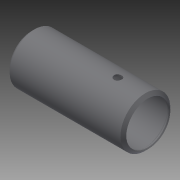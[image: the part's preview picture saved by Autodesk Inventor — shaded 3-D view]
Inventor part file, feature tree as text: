
AUTODESK INVENTOR PART (.ipt)
format: ipt  version: 2014 (Build 180170000, 170)  size: 142,336 bytes
history: native  units: in
note: dims shown in document units (in); Inventor stores cm internally (conversion verified against a paired STEP export)
features: other x56, revolve x2, sketch x2
ambient origin geometry x8: Origin, YZ Plane, XZ Plane, XY Plane, X Axis, Y Axis, Z Axis, Center Point
bodies: Solid1 (feature_tree)
feature tree (60):
  revolve  "Revolution1"  Angle=360.0deg
  revolve  "Revolution2"  [1 undecoded]
  other  "o1_XY"
  other  "o1_YZ"
  other  "o1_ZX"
  other  "o1_X"
  other  "o1_Y"
  other  "o1_Z"
  other  "o1_Center"
  other  "o2_XY"
  other  "o2_YZ"
  other  "o2_ZX"
  other  "o2_X"
  other  "o2_Y"
  other  "o2_Z"
  other  "o2_Center"
  other  "t1_XY"
  other  "t1_YZ"
  other  "t1_ZX"
  other  "t1_X"
  other  "t1_Y"
  other  "t1_Z"
  other  "t1_Center"
  other  "t2_XY"
  other  "t2_YZ"
  other  "t2_ZX"
  other  "t2_X"
  other  "t2_Y"
  other  "t2_Z"
  other  "t2_Center"
  other  "t3_XY"
  other  "t3_YZ"
  other  "t3_ZX"
  other  "t3_X"
  other  "t3_Y"
  other  "t3_Z"
  other  "t3_Center"
  other  "t4_XY"
  other  "t4_YZ"
  other  "t4_ZX"
  other  "t4_X"
  other  "t4_Y"
  other  "t4_Z"
  other  "t4_Center"
  other  "tube1_XY"
  other  "tube1_YZ"
  other  "tube1_ZX"
  other  "tube1_X"
  other  "tube1_Y"
  other  "tube1_Z"
  other  "tube1_Center"
  other  "tube2_XY"
  other  "tube2_YZ"
  other  "tube2_ZX"
  other  "tube2_X"
  other  "tube2_Y"
  other  "tube2_Z"
  other  "tube2_Center"
  sketch  "Sketch_5"
  sketch  "Sketch_1"  dims[d0=360.0deg d1=360.0deg]
note: 1 required parameter value undecoded (feature->parameter linkage not recoverable at this tier; creation-order binding heuristic only, values carry confidence <= 0.55)
